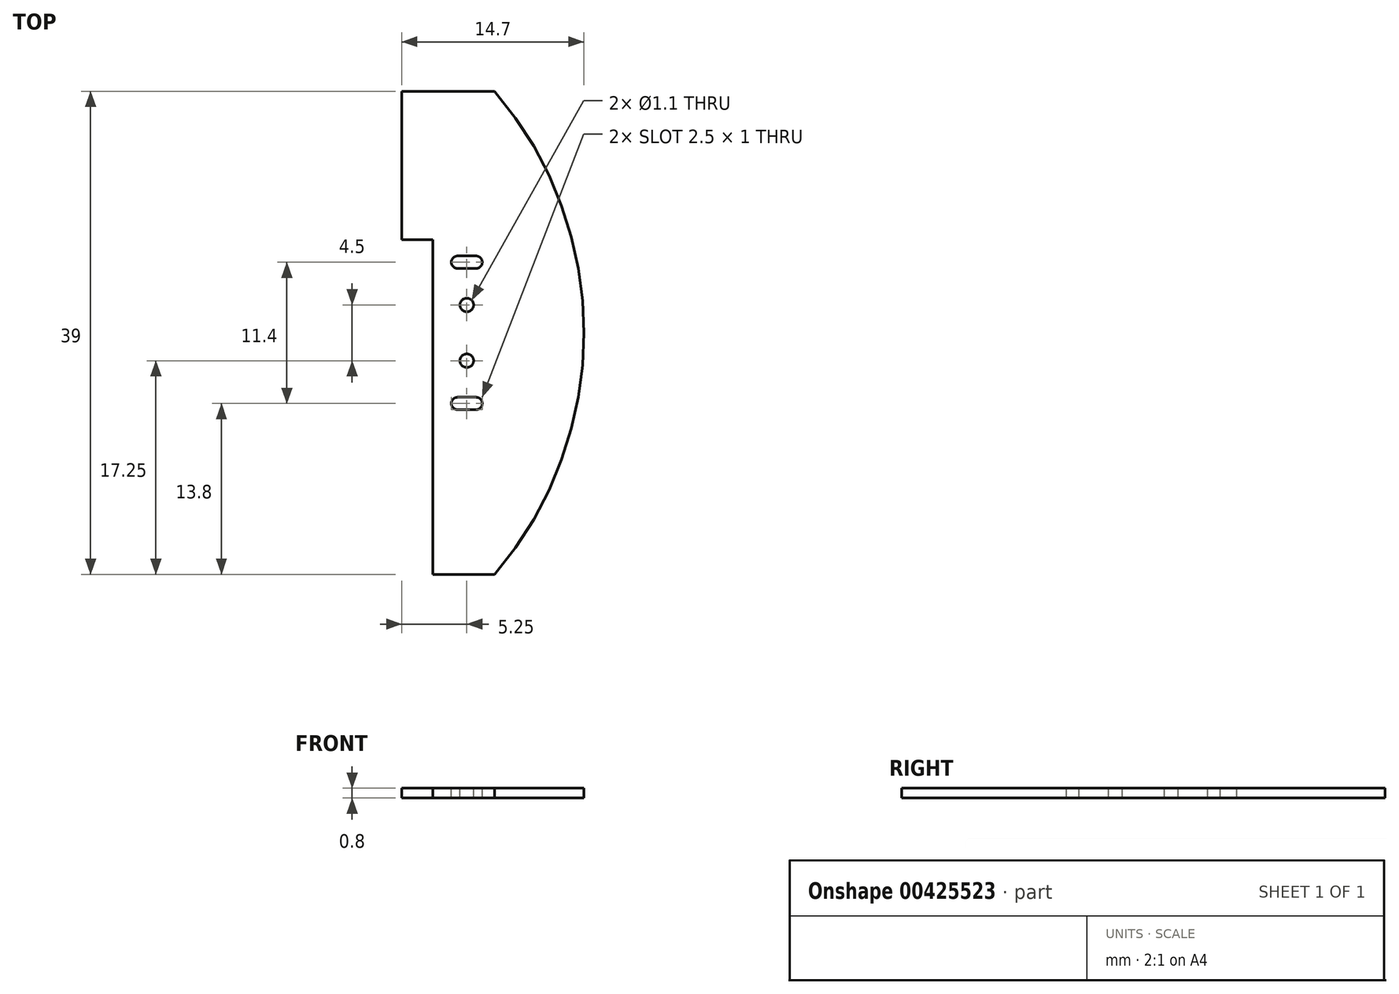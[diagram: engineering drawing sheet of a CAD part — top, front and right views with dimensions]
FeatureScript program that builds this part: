
annotation { "Feature Type Name" : "Feature", "Feature Type Description" : "" }
export const myFeature = defineFeature(function(context is Context, id is Id, definition is map)
    precondition{}
    {
        {
            var Q0;
            Q0=qCreatedBy(makeId("Top.planeOp"),FACE);
            var sketch = newSketch(context, id + "F0", { "sketchPlane" : qUnion([Q0])});
            skLineSegment(sketch, "E0.top", {"start": v(-2.5, 27) * mm, "end": v(5, 27) * mm});
            skLineSegment(sketch, "E0.left", {"start": v(-2.5, 15) * mm, "end": v(-2.5, 27) * mm});
            skLineSegment(sketch, "E1", {"start": v(0, 0) * mm, "end": v(0, -12) * mm});
            skLineSegment(sketch, "E2", {"start": v(0, -12) * mm, "end": v(5, -12) * mm});
            skArc(sketch, "E3", {"start": v(5, -12) * mm, "mid": v(12.2, 7.5) * mm, "end": v(5, 27) * mm});
            skLineSegment(sketch, "E4", {"start": v(-2.5, 15) * mm, "end": v(0, 15) * mm});
            skLineSegment(sketch, "E5", {"start": v(0, 15) * mm, "end": v(0, 0) * mm});
            skSolve(sketch);
        }
        {
            var Q0;
            Q0 = qSketchRegion(id + "F0", true);
            extrude(context, id + "F1", {"entities" : qUnion([Q0]), "depth" : .8 * mm});
        }
        {
            var Q0;
            Q0=makeQuery(id+"F1.opExtrude","CAP_FACE",FACE,{"disambiguationData":[OSD([sQuery(id+"F0.wireOp",EDGE,"E0.top"),sQuery(id+"F0.wireOp",EDGE,"E0.left"),sQuery(id+"F0.wireOp",EDGE,"E1"),sQuery(id+"F0.wireOp",EDGE,"E2"),sQuery(id+"F0.wireOp",EDGE,"E3"),sQuery(id+"F0.wireOp",EDGE,"E4"),sQuery(id+"F0.wireOp",EDGE,"E5")])],"isStart":false});
            var sketch = newSketch(context, id + "F2", { "sketchPlane" : qUnion([Q0])});
            skLineSegment(sketch, "E6", {"start": v(2.57, 7.5) * mm, "end": v(12.2, 7.5) * mm, "construction": true});
            skLineSegment(sketch, "E7", {"start": v(2.75, 17.88) * mm, "end": v(2.75, 10.04) * mm, "construction": true});
            skLineSegment(sketch, "E8", {"start": v(3.47, 9.75) * mm, "end": v(7.37, 9.75) * mm, "construction": true});
            skLineSegment(sketch, "E9.MirrorCS", {"start": v(3.47, 5.25) * mm, "end": v(7.37, 5.25) * mm, "construction": true});
            skCircle(sketch, "E10", {"center": v(2.75, 9.75) * mm, "radius": 0.55 * mm});
            skCircle(sketch, "E11.MirrorC", {"center": v(2.75, 5.25) * mm, "radius": 0.55 * mm});
            skLineSegment(sketch, "E12", {"start": v(3.65, 13.2) * mm, "end": v(9.13, 13.2) * mm, "construction": true});
            skLineSegment(sketch, "E13.bottom", {"start": v(3.5, 13.7) * mm, "end": v(2, 13.7) * mm});
            skLineSegment(sketch, "E13.top", {"start": v(3.5, 12.7) * mm, "end": v(2, 12.7) * mm});
            skLineSegment(sketch, "E13.left", {"start": v(4, 13.2) * mm, "end": v(4, 13.2) * mm});
            skLineSegment(sketch, "E13.right", {"start": v(1.5, 13.2) * mm, "end": v(1.5, 13.2) * mm});
            skPoint(sketch, "E13.middle", {"position": v(2.75, 13.2) * mm});
            skPoint(sketch, "E14.visualSharp", {"position": v(1.5, 12.7) * mm});
            skArc(sketch, "E14.filletArc", {"start": v(1.5, 13.2) * mm, "mid": v(1.65, 12.85) * mm, "end": v(2, 12.7) * mm});
            skPoint(sketch, "E15.visualSharp", {"position": v(1.5, 13.7) * mm});
            skArc(sketch, "E15.filletArc", {"start": v(2, 13.7) * mm, "mid": v(1.65, 13.55) * mm, "end": v(1.5, 13.2) * mm});
            skPoint(sketch, "E16.visualSharp", {"position": v(4, 13.7) * mm});
            skArc(sketch, "E16.filletArc", {"start": v(4, 13.2) * mm, "mid": v(3.85, 13.55) * mm, "end": v(3.5, 13.7) * mm});
            skPoint(sketch, "E17.visualSharp", {"position": v(4, 12.7) * mm});
            skArc(sketch, "E17.filletArc", {"start": v(3.5, 12.7) * mm, "mid": v(3.85, 12.85) * mm, "end": v(4, 13.2) * mm});
            skLineSegment(sketch, "E18.MirrorCS", {"start": v(3.5, 2.3) * mm, "end": v(2, 2.3) * mm});
            skArc(sketch, "E19.MirrorCS", {"start": v(3.5, 2.3) * mm, "mid": v(3.85, 2.15) * mm, "end": v(4, 1.8) * mm});
            skArc(sketch, "E20.MirrorCS", {"start": v(4, 1.8) * mm, "mid": v(3.85, 1.45) * mm, "end": v(3.5, 1.3) * mm});
            skLineSegment(sketch, "E21.MirrorCS", {"start": v(3.5, 1.3) * mm, "end": v(2, 1.3) * mm});
            skArc(sketch, "E22.MirrorCS", {"start": v(2, 1.3) * mm, "mid": v(1.65, 1.45) * mm, "end": v(1.5, 1.8) * mm});
            skArc(sketch, "E23.MirrorCS", {"start": v(1.5, 1.8) * mm, "mid": v(1.65, 2.15) * mm, "end": v(2, 2.3) * mm});
            skLineSegment(sketch, "E24.0", {"start": v(0, 15) * mm, "end": v(0, -12) * mm, "construction": true});
            skSolve(sketch);
        }
        {
            var Q0;
            Q0 = qSketchRegion(id + "F2", true);
            extrude(context, id + "F3", {"entities" : qUnion([Q0]), "operationType" : NewBodyOperationType.REMOVE, "oppositeDirection" : true, "depth" : 1 * mm});
        }
    });
